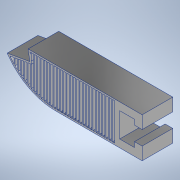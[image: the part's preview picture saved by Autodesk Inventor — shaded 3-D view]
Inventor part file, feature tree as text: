
AUTODESK INVENTOR PART (.ipt)
format: ipt  version: 2022 (Build 260153000, 153)  size: 431,616 bytes
history: native  units: mm
features: extrude x5, sketch x4, fillet x1, shell x1, projected_geometry x1
ambient origin geometry x8: Origin, YZ Plane, XZ Plane, XY Plane, X Axis, Y Axis, Z Axis, Center Point
bodies: Body1 (feature_tree)
feature tree (12):
  extrude  "Extrusion2"  Depth=5.8mm
  extrude  "Extrusion5"  Depth=12.0mm TaperAngle=0.0deg
  fillet  "Fillet2"  Radius=45.0mm
  shell  "Shell1"  Thickness=15.6mm
  extrude  "Extrusion7"  TaperAngle=0.0deg  [1 undecoded]
  extrude  "Extrusion8"  Depth=9.6mm
  extrude  "Extrusion9"  Depth=0.89mm
  sketch  "Sketch8"  dims[d41=5.8mm d48=44.0mm]
  sketch  "Sketch13"  dims[d50=3.0mm d56=12.0mm d57=0.0mm d63=45.0mm d67=15.6mm d71=0.0mm]
  sketch  "Sketch14"  dims[d80=17.453293mm d82=0.0mm d83=0.0mm]
  projected_geometry  "Projected Loop1"
  sketch  "Sketch15"  dims[d87=5.6mm d88=9.6mm d95=4.0mm d96=9.0mm d97=15.6mm d98=23.0mm d99=0.62mm d100=12.0mm d101=0.0mm d102=10.747401mm d103=12.0mm d104=0.0mm d105=0.38mm d106=3.81mm d107=0.38mm d1=0.38mm d108=0.38mm d109=0.38mm d110=0.38mm d111=0.38mm d112=0.38mm d113=0.38mm d116=3.81mm d117=3.81mm d118=0.38mm d119=0.38mm d120=3.81mm d121=3.81mm d122=3.81mm d123=3.81mm d124=3.81mm d125=3.81mm d126=3.81mm d127=12.0mm d128=0.0mm d129=0.38mm d131=0.38mm d132=0.38mm d133=0.38mm d134=0.38mm d135=0.38mm d136=0.38mm d137=0.38mm d138=0.38mm d139=0.38mm d140=0.38mm d151=0.38mm d154=0.89mm d155=0.89mm d156=0.89mm d157=0.38mm d158=0.89mm d159=0.89mm d160=0.89mm d161=0.38mm d162=0.89mm d163=0.38mm d164=0.89mm d165=0.89mm d166=0.38mm d167=0.89mm d168=0.89mm d169=0.38mm d170=0.89mm d171=0.89mm d172=0.38mm d173=0.89mm d174=0.89mm d175=0.38mm d176=0.89mm d178=0.38mm d179=0.89mm d180=0.89mm d181=0.38mm d182=0.89mm d183=0.89mm d184=0.89mm]
note: 1 required parameter value undecoded (feature->parameter linkage not recoverable at this tier; creation-order binding heuristic only, values carry confidence <= 0.55)
